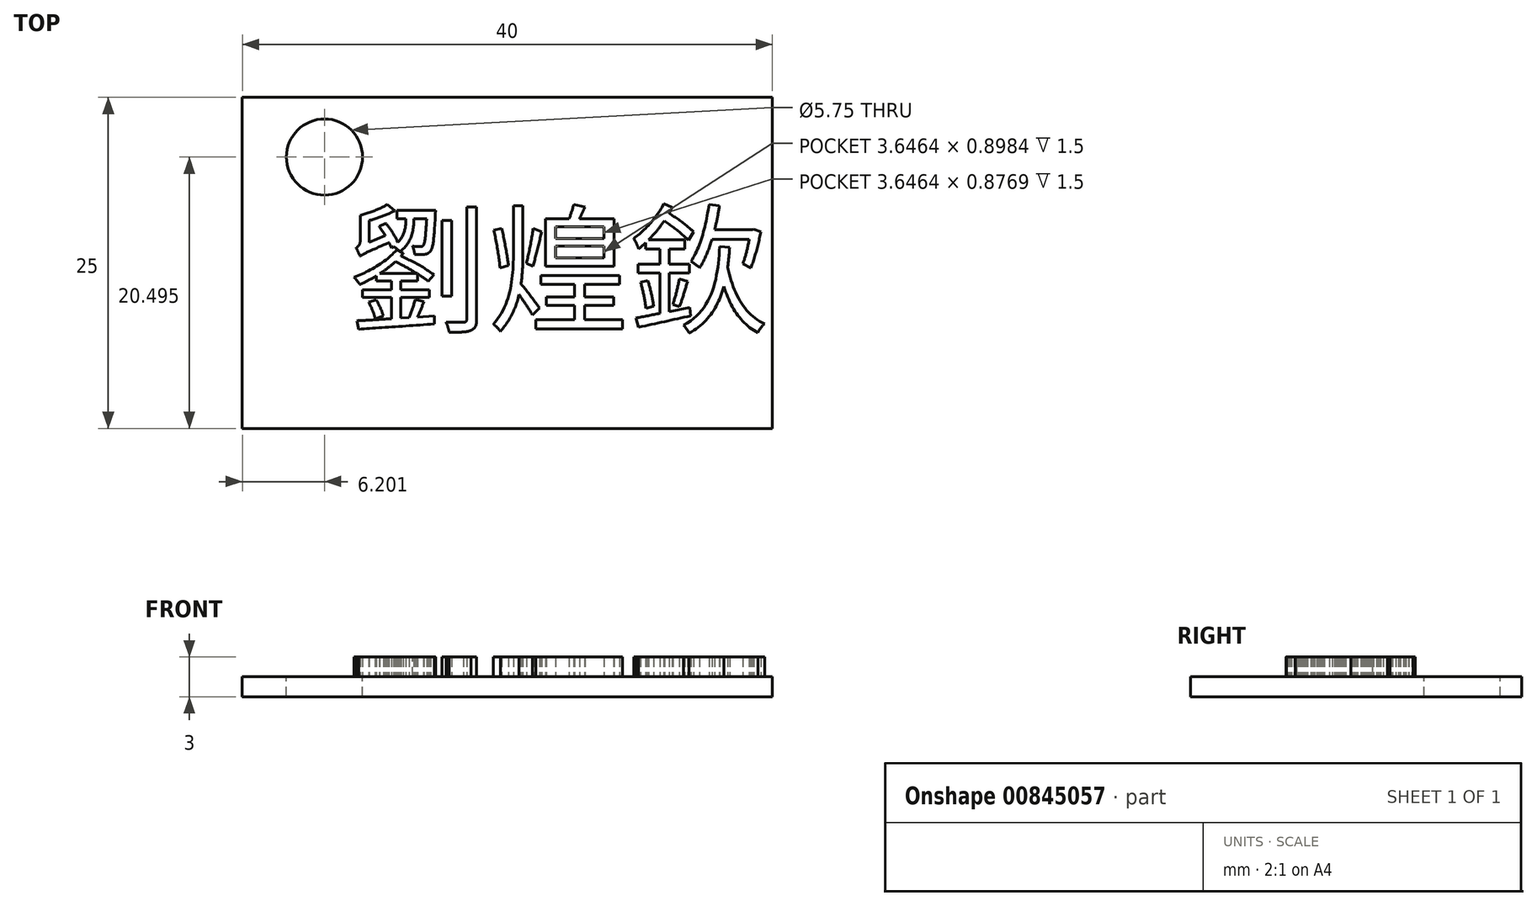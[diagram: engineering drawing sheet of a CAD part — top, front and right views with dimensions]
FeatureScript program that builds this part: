
annotation { "Feature Type Name" : "Feature", "Feature Type Description" : "" }
export const myFeature = defineFeature(function(context is Context, id is Id, definition is map)
    precondition{}
    {
        {
            var Q0;
            Q0=qCreatedBy(makeId("Top.planeOp"),FACE);
            var sketch = newSketch(context, id + "F0", { "sketchPlane" : qUnion([Q0])});
            skLineSegment(sketch, "E0.bottom", {"start": v(-56.22, 47.93) * mm, "end": v(-16.22, 47.93) * mm});
            skLineSegment(sketch, "E0.top", {"start": v(-56.22, 22.93) * mm, "end": v(-16.22, 22.93) * mm});
            skLineSegment(sketch, "E0.left", {"start": v(-56.22, 47.93) * mm, "end": v(-56.22, 22.93) * mm});
            skLineSegment(sketch, "E0.right", {"start": v(-16.22, 47.93) * mm, "end": v(-16.22, 22.93) * mm});
            skSolve(sketch);
        }
        {
            var Q0;
            Q0=makeQuery(id+"F0.imprint","IMPRINT",FACE,{"disambiguationData":[TD([[makeQuery(id+"F0.imprint","IMPRINT",EDGE,{"derivedFrom":sQuery(id+"F0.wireOp",EDGE,"E0.bottom")}),-1.0]])]});
            extrude(context, id + "F1", {"entities" : qUnion([Q0]), "depth" : 1.5 * mm, "offsetDistance" : 25 * mm});
        }
        {
            var Q0;
            Q0=makeQuery(id+"F1.opExtrude","CAP_FACE",FACE,{"disambiguationData":[OSD([sQuery(id+"F0.wireOp",EDGE,"E0.bottom"),sQuery(id+"F0.wireOp",EDGE,"E0.top"),sQuery(id+"F0.wireOp",EDGE,"E0.left"),sQuery(id+"F0.wireOp",EDGE,"E0.right")])],"isStart":false});
            var sketch = newSketch(context, id + "F2", { "sketchPlane" : qUnion([Q0])});
            skText(sketch, "E1", { "text": "劉煌欽", "fontName": "NotoSansCJKtc-Regular.otf"});
            const initialGuessF2  = {"E1": [-0.04822, 0.031, 1, 0, 0.00761]};
            skSetInitialGuess(sketch, initialGuessF2);
            skSolve(sketch);
        }
        {
            var Q0;
            Q0 = qSketchRegion(id + "F2", true);
            extrude(context, id + "F3", {"entities" : qUnion([Q0]), "operationType" : NewBodyOperationType.ADD, "depth" : 1.5 * mm, "offsetDistance" : 25 * mm});
        }
        {
            var Q0;
            {var subQ0=sQuery(id+"F0.wireOp",EDGE,"E0.left");var subQ1=sQuery(id+"F0.wireOp",EDGE,"E0.top");var subQ2=sQuery(id+"F0.wireOp",EDGE,"E0.right");var subQ3=sQuery(id+"F0.wireOp",EDGE,"E0.bottom");Q0=makeQuery(id+"F3.boolean.opBoolean","SPLIT",FACE,{"disambiguationData":[TD([makeQuery(id+"F1.opExtrude","SWEPT_FACE",FACE,{"disambiguationData":[OSD([subQ3])]})])],"derivedFrom":makeQuery(id+"F1.opExtrude","CAP_FACE",FACE,{"disambiguationData":[OSD([subQ3,subQ1,subQ0,subQ2])],"isStart":false})});}
            var sketch = newSketch(context, id + "F4", { "sketchPlane" : qUnion([Q0])});
            skCircle(sketch, "E2", {"center": v(-50.02, 43.43) * mm, "radius": 2.87 * mm});
            skSolve(sketch);
        }
        {
            var Q0;
            Q0=makeQuery(id+"F4.imprint","IMPRINT",FACE,{"disambiguationData":[TD([[makeQuery(id+"F4.imprint","IMPRINT",EDGE,{"derivedFrom":sQuery(id+"F4.wireOp",EDGE,"E2")}),1.0]])]});
            extrude(context, id + "F5", {"entities" : qUnion([Q0]), "operationType" : NewBodyOperationType.REMOVE, "oppositeDirection" : true, "depth" : 2 * mm, "offsetDistance" : 25 * mm});
        }
    });
